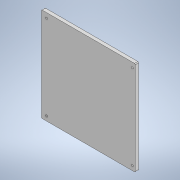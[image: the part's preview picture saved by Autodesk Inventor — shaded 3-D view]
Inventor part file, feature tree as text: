
AUTODESK INVENTOR PART (.ipt)
format: ipt  version: 2020.2 (Build 242310000, 310)  size: 115,200 bytes
history: native  units: mm
features: sketch x2, extrude x1, hole x1, fillet x1
ambient origin geometry x8: Origin, YZ Plane, XZ Plane, XY Plane, X Axis, Y Axis, Z Axis, Center Point
bodies: Solide1 (feature_tree)
feature tree (5):
  extrude  "Extrusion1"  Depth=170.0mm
  hole  "Perçage1"  [1 undecoded]
  fillet  "Congé2"  Radius=6.0mm
  sketch  "Esquisse1"
  sketch  "Esquisse2"
note: 1 required parameter value undecoded (feature->parameter linkage not recoverable at this tier; creation-order binding heuristic only, values carry confidence <= 0.55)
